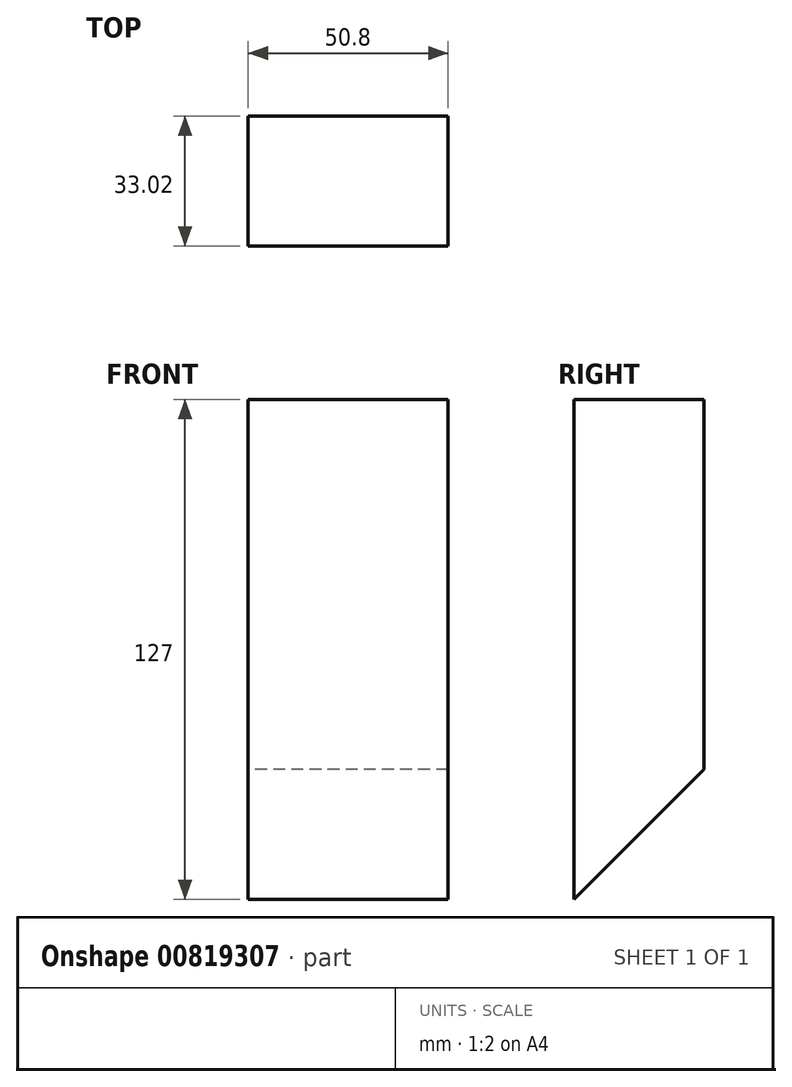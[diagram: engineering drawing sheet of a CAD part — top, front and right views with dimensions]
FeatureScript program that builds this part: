
annotation { "Feature Type Name" : "Feature", "Feature Type Description" : "" }
export const myFeature = defineFeature(function(context is Context, id is Id, definition is map)
    precondition{}
    {
        {
            var Q0;
            Q0=qCreatedBy(makeId("Front.planeOp"),FACE);
            var sketch = newSketch(context, id + "F0", { "sketchPlane" : qUnion([Q0])});
            skLineSegment(sketch, "E0.bottom", {"start": v(-25.4, 63.5) * mm, "end": v(25.4, 63.5) * mm});
            skLineSegment(sketch, "E0.top", {"start": v(-25.4, -63.5) * mm, "end": v(25.4, -63.5) * mm});
            skLineSegment(sketch, "E0.left", {"start": v(-25.4, 63.5) * mm, "end": v(-25.4, -63.5) * mm});
            skLineSegment(sketch, "E0.right", {"start": v(25.4, 63.5) * mm, "end": v(25.4, -63.5) * mm});
            skPoint(sketch, "E0.middle", {"position": v(0, 0) * mm});
            skSolve(sketch);
        }
        {
            var Q0;
            Q0=makeQuery(id+"F0.imprint","IMPRINT",FACE,{"disambiguationData":[TD([[makeQuery(id+"F0.imprint","IMPRINT",EDGE,{"derivedFrom":sQuery(id+"F0.wireOp",EDGE,"E0.bottom")}),-1.0]])]});
            extrude(context, id + "F1", {"entities" : qUnion([Q0]), "depth" : 33.02 * mm, "offsetDistance" : 25.4 * mm});
        }
        {
            var Q0;
            Q0=makeQuery(id+"F1.opExtrude","CAP_EDGE",EDGE,{"disambiguationData":[OSD([sQuery(id+"F0.wireOp",EDGE,"E0.top")])],"isStart":true});
            chamfer(context, id + "F2", {"entities" : qUnion([Q0]), "width" : 33.02 * mm, "tangentPropagation" : true});
        }
    });
